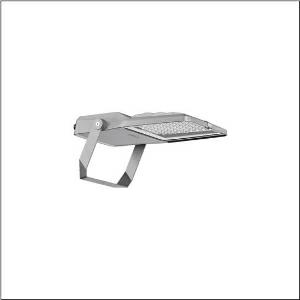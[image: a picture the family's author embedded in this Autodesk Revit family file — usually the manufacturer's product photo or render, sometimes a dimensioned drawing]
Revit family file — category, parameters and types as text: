
# Revit family: floodlight_fl_21_mini___pl61_5xa7776c4c1a_3fb0
name_source: partatom
category: Lighting Fixtures
units: mm (PartAtom-declared; Revit-internal decimal feet)

## family parameters
Cut with Voids When Loaded = No
Host = Face
Light Source = No
Part Type = Normal
Room Calculation Point = No
Round Connector Dimension = Use Diameter
Shared = No

## types (1)
- --- (1 x LED, 12460 lm, 89 W, 4000K)
    Apparent Load = 89 VA
    CIE Flux Codes = 33 65 98 100 100
    Color Rendering = 70
    Color Temperature = 4000K
    Default Elevation = 1800 mm
    Description = Floodlight FL 21 mini, floodlight, primary light control with lens, of PMMA, primary optical cover: protective disc, of toughened safety glass, transparent, light distribution: PL61, light emission: direct distribution, installation type: surface-mounted, LED, High Power LED, rated luminous flux: 12.460lm, luminous efficacy: 140lm/W, light colour: 740, colour temperature: 4000K, control gear: D4iSmart Interface (Zhaga), control: overheat protection, constant luminous flux control, time-dependent luminous flux control, flexible luminous flux parameterisation, pre-setting: logarithmic dimming characteristic, with terminal, 6-pole, mains connection: 220..240V, AC, 50/60Hz, start of lifetime: 89W, end of service life: 94W, reduction: 43W, mounting bracket, of diecast aluminium, powder-coated, SITECO metallic grey (DB 702S), corrosivity category C5 mid according to DIN EN ISO 12944, suitable for swimming pools, chlorine-resistant, sealing non-destructively replaceable, mounting bracket, of steel, galvanised, powder-coated, SITECO metallic grey (DB 702S), Smart Interface below and above, protection rating (complete): IP66, insulation class (complete): insulation class II (safety insulation), certification: CE, ENEC, VDE, protection symbol: D, impact resistance: IK08, permissible operating ambient temperature: -40..+40°C, permissible operating ambient temperature for outdoor applications: -40..+50°C, standard: DIN EN 12944, LABS conformity tested according to VDMA 24364:2018-05, packaging unit: 1 piece

Light Distribution: PL61
    Height = 70 mm
    Lamp = 1 x LED
    Lamp Light Flux = 12460 lm
    Lamp Power = 89 W
    Lamp count = 1
    Length = 485 mm
    Luminous efficacy = 140 lm/W
    Manufacturer = Siteco
    ModVariant = No
    Model = 5XA7776C4C1A
    Number of Poles = 1
    OnlyDefault = Yes
    Power Factor = 1
    Product Name = Floodlight FL 21 mini | PL61
    Product group = floodlight | pylon annexe
    ProductGroupID = 6201
    Protection Class = Protection class II
    Protection Degree = IP 66
    RLX_Detail_Level = 1
    RLX_Emergency_Light_Flux = 0 lm
    RLX_Emergency_Type = 0
    RLX_Emergency_Type_DB = No
    RlxData = <blob elided: 96005 chars, md5=7dff2bec>
    Socket = socket
    Standby Power = 0 W
    System Light Flux = 12460 lm
    System Power = 89 W
    Type Comments = factory setting: luminous flux: 100 % | dim-lin: 254 | 456 mA
    Type Image = l_1006845.jpg
    URL = http://relux.com
    VarID = @adj_102121
    Voltage = 0 V
    Weight = 0.00 kg
    Width = 337 mm

## geometry (parser evidence)
native form markers: Blend x4, Sweep x15
no freeform markers — native parametric forms only
